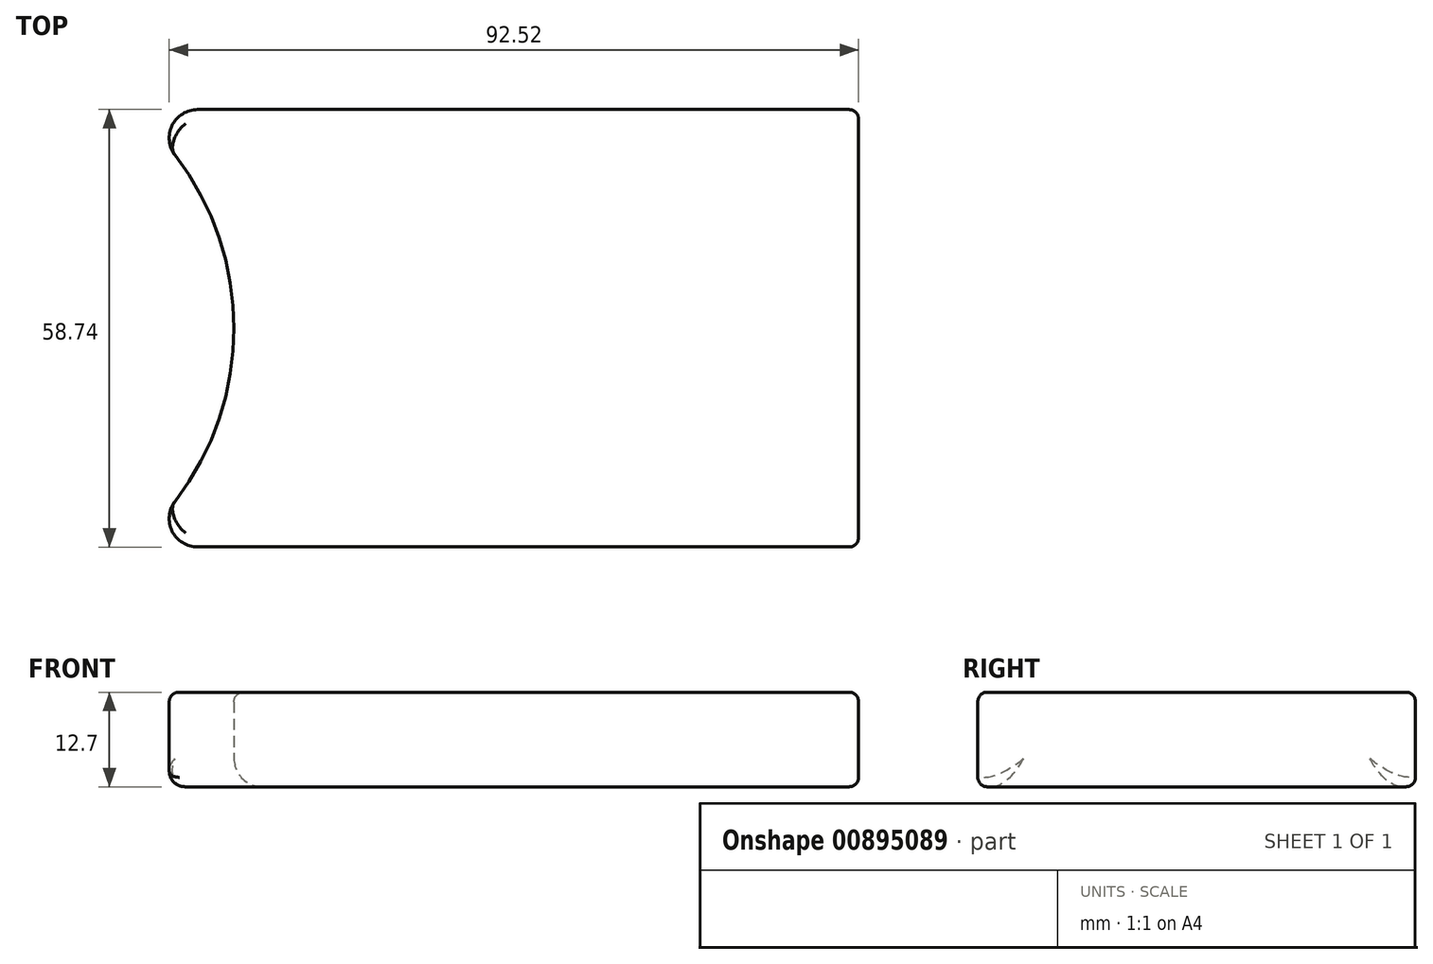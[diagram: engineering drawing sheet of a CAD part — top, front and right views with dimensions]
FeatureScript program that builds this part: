
annotation { "Feature Type Name" : "Feature", "Feature Type Description" : "" }
export const myFeature = defineFeature(function(context is Context, id is Id, definition is map)
    precondition{}
    {
        {
            var Q0;
            Q0=qCreatedBy(makeId("Top.planeOp"),FACE);
            var sketch = newSketch(context, id + "F0", { "sketchPlane" : qUnion([Q0])});
            skLineSegment(sketch, "E0.bottom", {"start": v(0, 29.37) * mm, "end": v(101.6, 29.37) * mm});
            skLineSegment(sketch, "E0.top", {"start": v(0, -29.37) * mm, "end": v(101.6, -29.37) * mm});
            skLineSegment(sketch, "E0.left", {"start": v(0, 29.37) * mm, "end": v(0, -29.37) * mm});
            skLineSegment(sketch, "E0.right", {"start": v(101.6, 29.37) * mm, "end": v(101.6, -29.37) * mm});
            skSolve(sketch);
        }
        {
            var Q0;
            Q0 = qSketchRegion(id + "F2", true);
            var Q1;
            Q1 = qSketchRegion(id + "F0", true);
            extrude(context, id + "F1", {"entities" : qUnion([Q0, Q1]), "depth" : 12.7 * mm, "offsetDistance" : 25.4 * mm});
        }
        {
            var Q0;
            Q0=qCreatedBy(makeId("Top.planeOp"),FACE);
            var sketch = newSketch(context, id + "F2", { "sketchPlane" : qUnion([Q0])});
            skCircle(sketch, "E1", {"center": v(-20.32, 0) * mm, "radius": 38.1 * mm});
            skSolve(sketch);
        }
        {
            var Q0;
            Q0 = qSketchRegion(id + "F2", true);
            extrude(context, id + "F3", {"entities" : qUnion([Q0]), "depth" : 25.4 * mm, "offsetDistance" : 25.4 * mm});
        }
        {
            var Q0;
            Q0=makeQuery(id+"F3.opExtrude","SWEPT_BODY",BODY,{"disambiguationData":[OSD([sQuery(id+"F2.wireOp",EDGE,"E1")])]});
            var Q1;
            Q1=makeQuery(id+"F1.opExtrude","SWEPT_BODY",BODY,{"disambiguationData":[OSD([sQuery(id+"F0.wireOp",EDGE,"E0.bottom"),sQuery(id+"F0.wireOp",EDGE,"E0.top"),sQuery(id+"F0.wireOp",EDGE,"E0.left"),sQuery(id+"F0.wireOp",EDGE,"E0.right")])]});
            booleanBodies(context, id + "F4", {"operationType" : BooleanOperationType.SUBTRACTION, "tools" : qUnion([Q0]), "targets" : qUnion([Q1])});
        }
        {
            var Q0;
            Q0=makeQuery(id+"F1.opExtrude","CAP_EDGE",EDGE,{"disambiguationData":[OSD([sQuery(id+"F0.wireOp",EDGE,"E0.right")])],"isStart":true});
            var Q1;
            Q1=makeQuery(id+"F1.opExtrude","CAP_EDGE",EDGE,{"disambiguationData":[OSD([sQuery(id+"F0.wireOp",EDGE,"E0.right")])],"isStart":false});
            var Q2;
            Q2=makeQuery(id+"F1.opExtrude","SWEPT_EDGE",EDGE,{"disambiguationData":[OSD([sQuery(id+"F0.wireOp",EDGE,"E0.bottom"),sQuery(id+"F0.wireOp",EDGE,"E0.right")])]});
            var Q3;
            Q3=makeQuery(id+"F1.opExtrude","SWEPT_EDGE",EDGE,{"disambiguationData":[OSD([sQuery(id+"F0.wireOp",EDGE,"E0.top"),sQuery(id+"F0.wireOp",EDGE,"E0.right")])]});
            var Q4;
            Q4=makeQuery(id+"F1.opExtrude","CAP_EDGE",EDGE,{"disambiguationData":[OSD([sQuery(id+"F0.wireOp",EDGE,"E0.top")])],"isStart":true});
            var Q5;
            Q5=makeQuery(id+"F1.opExtrude","CAP_EDGE",EDGE,{"disambiguationData":[OSD([sQuery(id+"F0.wireOp",EDGE,"E0.bottom")])],"isStart":true});
            var Q6;
            Q6=makeQuery(id+"F1.opExtrude","CAP_EDGE",EDGE,{"disambiguationData":[OSD([sQuery(id+"F0.wireOp",EDGE,"E0.bottom")])],"isStart":false});
            var Q7;
            Q7=makeQuery(id+"F1.opExtrude","CAP_EDGE",EDGE,{"disambiguationData":[OSD([sQuery(id+"F0.wireOp",EDGE,"E0.top")])],"isStart":false});
            var Q8;
            Q8=makeQuery(id+"F4.opBoolean","COPY",EDGE,{"derivedFrom":makeQuery(id+"F3.opExtrude","CAP_EDGE",EDGE,{"disambiguationData":[OSD([sQuery(id+"F2.wireOp",EDGE,"E1")])],"isStart":true})});
            var Q9;
            Q9=makeQuery(id+"F4.opBoolean","INTERSECT",EDGE,{"derivedFrom":[makeQuery(id+"F1.opExtrude","CAP_FACE",FACE,{"disambiguationData":[OSD([sQuery(id+"F0.wireOp",EDGE,"E0.bottom"),sQuery(id+"F0.wireOp",EDGE,"E0.top"),sQuery(id+"F0.wireOp",EDGE,"E0.left"),sQuery(id+"F0.wireOp",EDGE,"E0.right")])],"isStart":false}),makeQuery(id+"F3.opExtrude","SWEPT_FACE",FACE,{"disambiguationData":[OSD([sQuery(id+"F2.wireOp",EDGE,"E1")])]})]});
            fillet(context, id + "F5", {"entities" : qUnion([Q0, Q1, Q2, Q3, Q4, Q5, Q6, Q7, Q8, Q9]), "radius" : 1.27 * mm, "tangentPropagation" : true, "allowEdgeOverflow" : false});
        }
        {
            var Q0;
            Q0=makeQuery(id+"F4.opBoolean","INTERSECT",EDGE,{"derivedFrom":[makeQuery(id+"F1.opExtrude","SWEPT_FACE",FACE,{"disambiguationData":[OSD([sQuery(id+"F0.wireOp",EDGE,"E0.bottom")])]}),makeQuery(id+"F3.opExtrude","SWEPT_FACE",FACE,{"disambiguationData":[OSD([sQuery(id+"F2.wireOp",EDGE,"E1")])]})]});
            var Q1;
            Q1=makeQuery(id+"F4.opBoolean","INTERSECT",EDGE,{"derivedFrom":[makeQuery(id+"F1.opExtrude","SWEPT_FACE",FACE,{"disambiguationData":[OSD([sQuery(id+"F0.wireOp",EDGE,"E0.top")])]}),makeQuery(id+"F3.opExtrude","SWEPT_FACE",FACE,{"disambiguationData":[OSD([sQuery(id+"F2.wireOp",EDGE,"E1")])]})]});
            fillet(context, id + "F6", {"entities" : qUnion([Q0, Q1]), "radius" : 3.8 * mm, "tangentPropagation" : true, "allowEdgeOverflow" : false});
        }
    });
